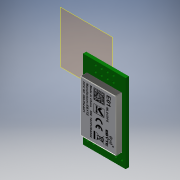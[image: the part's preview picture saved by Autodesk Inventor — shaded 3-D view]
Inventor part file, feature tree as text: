
AUTODESK INVENTOR PART (.ipt)
format: ipt  version: 2019 (Build 230136000, 136)  size: 1,094,144 bytes
history: native  units: in
note: dims shown in document units (in); Inventor stores cm internally (conversion verified against a paired STEP export)
features: other x3, sketch x3, extrude x2, plane x1, fillet x1, projected_geometry x1
ambient origin geometry x8: Origin, YZ Plane, XZ Plane, XY Plane, X Axis, Y Axis, Z Axis, Center Point
bodies: Solid1 (feature_tree)
feature tree (11):
  other  "E01-ML01DP5, E01-ML01DP5_23"
  plane  "Work Plane1"
  extrude  "Extrusion2"  Depth=0.054in TaperAngle=0.0deg
  extrude  "Extrusion3"  Depth=0.869in
  fillet  "Fillet1"  Radius=0.2075in
  other  "Decal1"
  sketch  "Sketch2"  dims[d3=1.3175in d4=0.054in d5=0.0in]
  sketch  "Sketch3"  dims[d6=0.5925in d7=0.869in d8=0.2075in]
  projected_geometry  "Projected Loop1"
  sketch  "Sketch4"  dims[d9=0.06in d10=0.1045in d11=0.0in d12=0.009in]
  other  "Image1"
